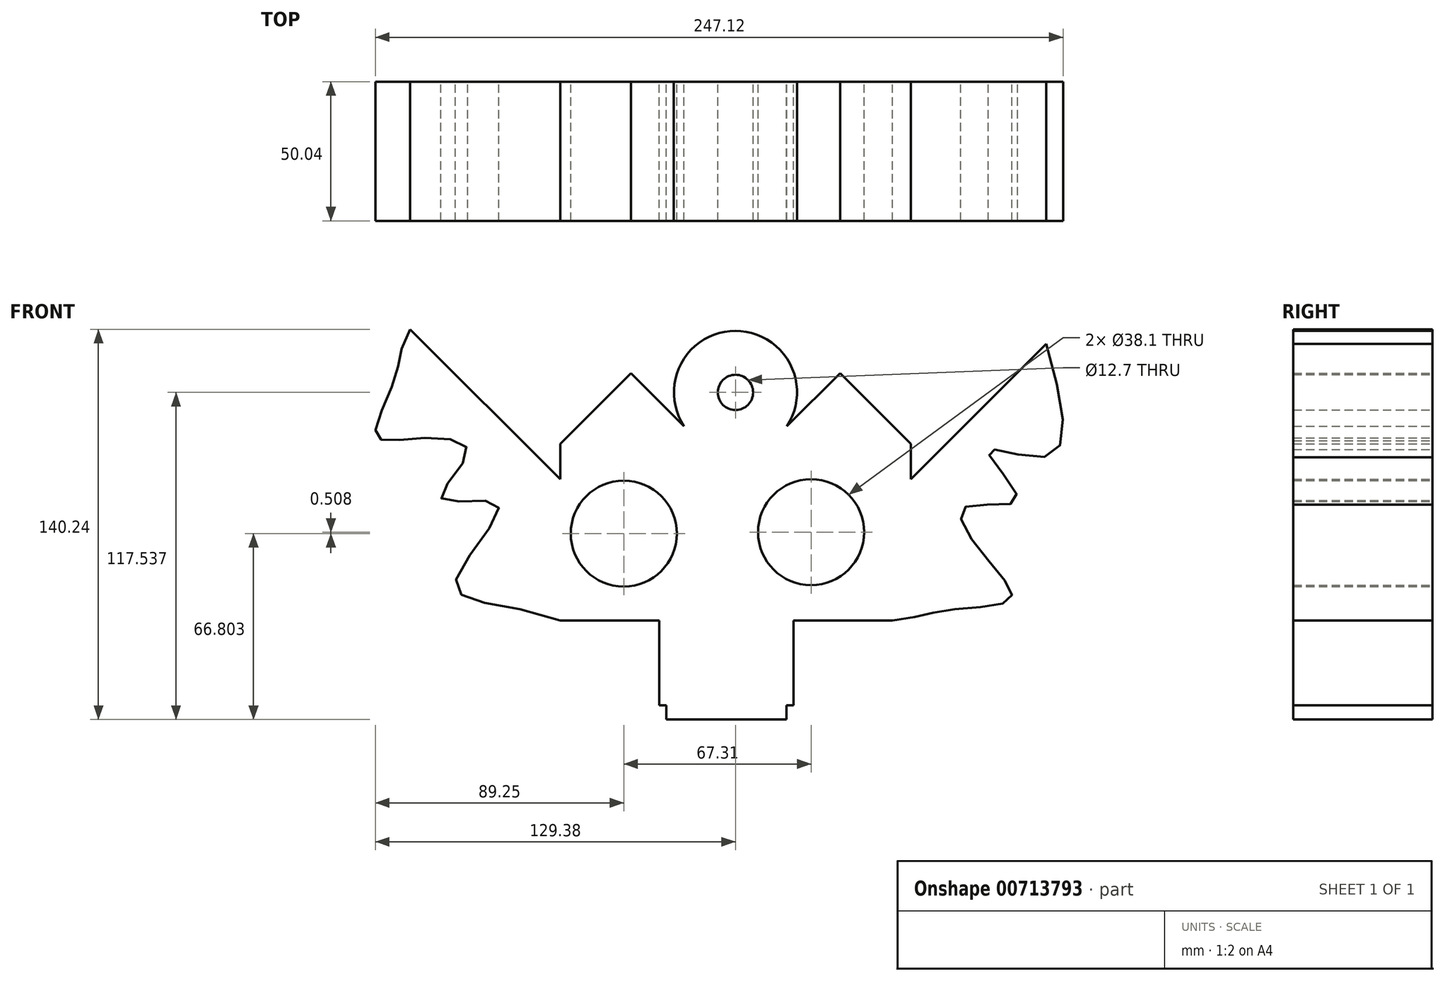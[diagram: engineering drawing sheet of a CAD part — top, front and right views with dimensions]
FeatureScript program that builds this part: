
annotation { "Feature Type Name" : "Feature", "Feature Type Description" : "" }
export const myFeature = defineFeature(function(context is Context, id is Id, definition is map)
    precondition{}
    {
        {
            var Q0;
            Q0=qCreatedBy(makeId("Front.planeOp"),FACE);
            var sketch = newSketch(context, id + "F0", { "sketchPlane" : qUnion([Q0])});
            skLineSegment(sketch, "E0", {"start": v(-18.44, -19.29) * mm, "end": v(-18.44, -49.77) * mm});
            skLineSegment(sketch, "E1", {"start": v(-18.44, -49.77) * mm, "end": v(-15.9, -49.77) * mm});
            skLineSegment(sketch, "E2", {"start": v(29.82, -19.29) * mm, "end": v(29.82, -49.77) * mm});
            skLineSegment(sketch, "E3", {"start": v(29.82, -49.77) * mm, "end": v(27.28, -49.77) * mm});
            skLineSegment(sketch, "E4", {"start": v(-15.9, -49.77) * mm, "end": v(-15.9, -54.85) * mm});
            skLineSegment(sketch, "E5", {"start": v(27.28, -49.77) * mm, "end": v(27.28, -54.85) * mm});
            skLineSegment(sketch, "E6", {"start": v(-15.9, -54.85) * mm, "end": v(27.28, -54.85) * mm});
            skLineSegment(sketch, "E7", {"start": v(-18.44, -19.29) * mm, "end": v(-54, -19.29) * mm});
            skLineSegment(sketch, "E8", {"start": v(29.82, -19.29) * mm, "end": v(65.38, -19.29) * mm});
            skLineSegment(sketch, "E9", {"start": v(-107.88, 85.4) * mm, "end": v(-54, 31.51) * mm});
            skLineSegment(sketch, "E10", {"start": v(71.98, 31.51) * mm, "end": v(125.86, 85.4) * mm});
            skFitSpline(sketch, "E11", {"points": [v(-107.88, 85.4) * mm, v(-113.33, 67.92) * mm, v(-120.15, 47.16) * mm, v(-104.34, 46.23) * mm, v(-87.3, 41.27) * mm, v(-96.6, 24.53) * mm, v(-76.45, 22.36) * mm, v(-91.63, -5.84) * mm, v(-54, -19.29) * mm], "startDerivative": vector(-117.26, -187.26) * mm, "endDerivative": vector(334.54, -128.82) * mm});
            skFitSpline(sketch, "E12", {"points": [v(65.38, -19.29) * mm, v(85.95, -15.44) * mm, v(107.96, -11.42) * mm, v(97.75, 4.86) * mm, v(91.35, 21.42) * mm, v(110.3, 24.18) * mm, v(99.8, 41.51) * mm, v(121.7, 39.9) * mm, v(119.3, 84.62) * mm], "startDerivative": vector(220, 20.33) * mm, "endDerivative": vector(-100.47, 344.12) * mm});
            skLineSegment(sketch, "E13", {"start": v(-54, 31.51) * mm, "end": v(-54, 44.21) * mm});
            skLineSegment(sketch, "E14", {"start": v(71.98, 31.51) * mm, "end": v(71.98, 44.21) * mm});
            skLineSegment(sketch, "E15", {"start": v(-54, 44.21) * mm, "end": v(-28.6, 69.61) * mm});
            skLineSegment(sketch, "E16", {"start": v(71.98, 44.21) * mm, "end": v(46.58, 69.61) * mm});
            skLineSegment(sketch, "E17", {"start": v(-28.6, 69.61) * mm, "end": v(-3.2, 44.21) * mm});
            skLineSegment(sketch, "E18", {"start": v(21.18, 44.21) * mm, "end": v(46.58, 69.61) * mm});
            skArc(sketch, "E19", {"start": v(21.18, 44.21) * mm, "mid": v(9, 84.82) * mm, "end": v(-3.2, 44.21) * mm});
            skCircle(sketch, "E20", {"center": v(9, 62.69) * mm, "radius": 6.35 * mm});
            skLineSegment(sketch, "E21", {"start": v(-18.44, -19.29) * mm, "end": v(-31.14, -19.29) * mm});
            skLineSegment(sketch, "E22", {"start": v(29.82, -19.29) * mm, "end": v(36.17, -19.29) * mm});
            skCircle(sketch, "E23", {"center": v(-31.14, 11.95) * mm, "radius": 19.05 * mm});
            skCircle(sketch, "E24", {"center": v(36.17, 12.46) * mm, "radius": 19.05 * mm});
            skSolve(sketch);
        }
        {
            var Q0;
            Q0 = qSketchRegion(id + "F0", true);
            extrude(context, id + "F1", {"entities" : qUnion([Q0]), "depth" : 50.04 * mm, "offsetDistance" : 25.4 * mm});
        }
    });
